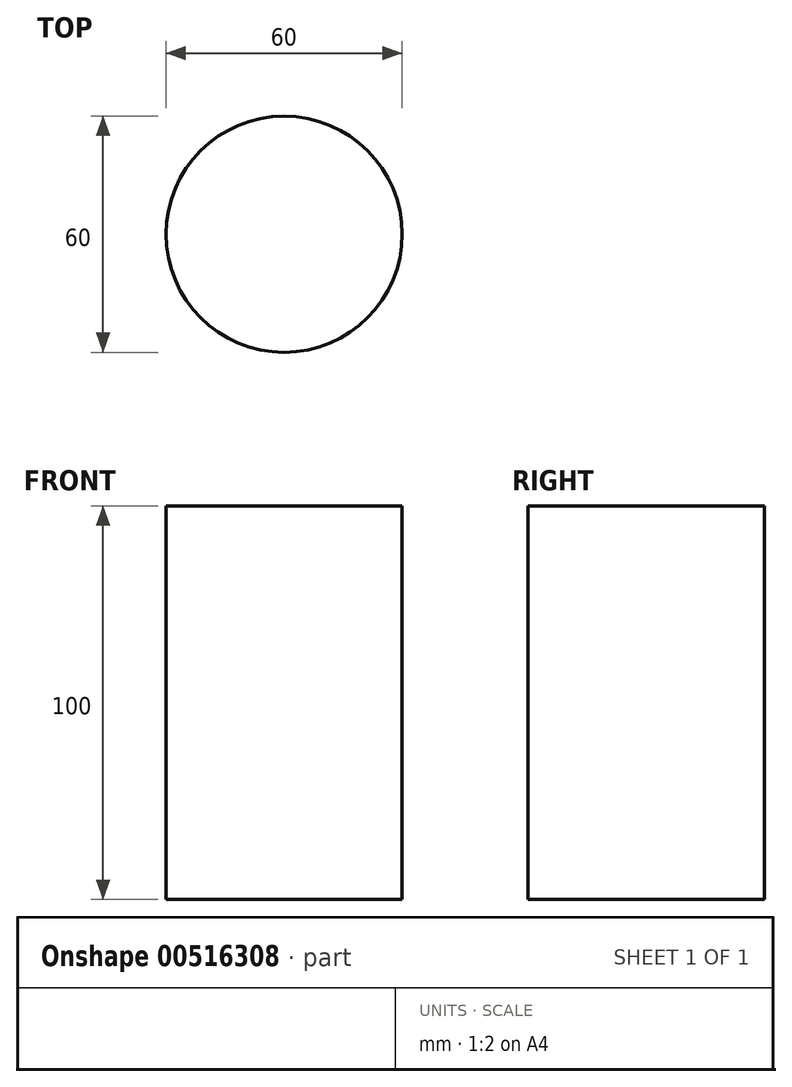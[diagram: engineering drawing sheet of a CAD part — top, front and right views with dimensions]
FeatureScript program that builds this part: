
annotation { "Feature Type Name" : "Feature", "Feature Type Description" : "" }
export const myFeature = defineFeature(function(context is Context, id is Id, definition is map)
    precondition{}
    {
        {
            var Q0;
            Q0=qCreatedBy(makeId("Top.planeOp"),FACE);
            var sketch = newSketch(context, id + "F0", { "sketchPlane" : qUnion([Q0])});
            skCircle(sketch, "E0", {"center": v(0, 0) * mm, "radius": 30 * mm});
            skSolve(sketch);
        }
        {
            var Q0;
            Q0 = qSketchRegion(id + "F0", true);
            extrude(context, id + "F1", {"entities" : qUnion([Q0]), "depth" : 100 * mm, "offsetDistance" : 25 * mm});
        }
    });
